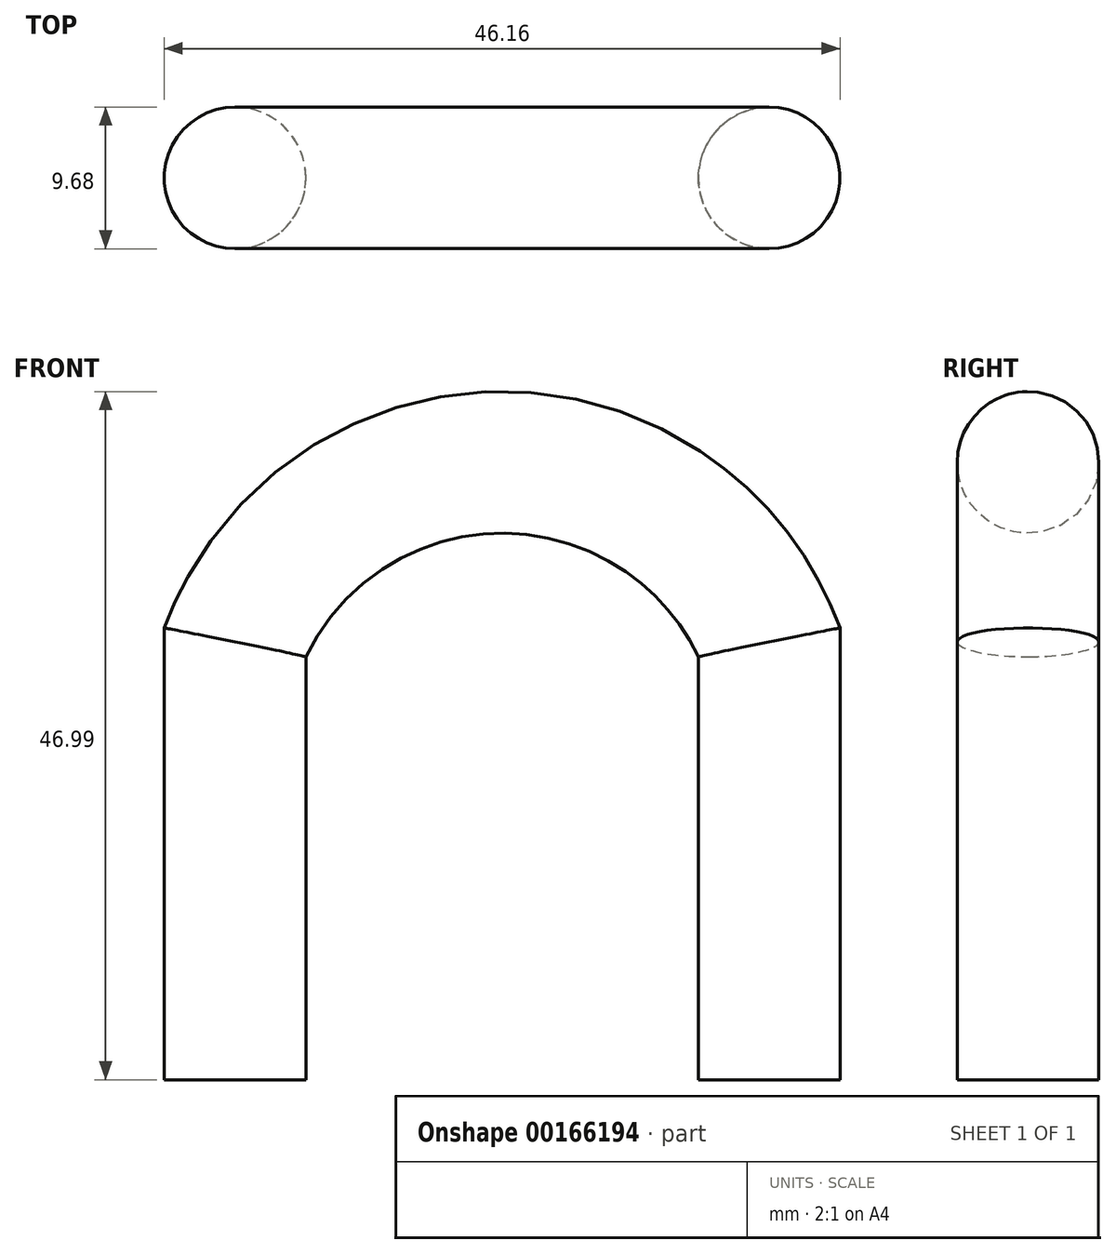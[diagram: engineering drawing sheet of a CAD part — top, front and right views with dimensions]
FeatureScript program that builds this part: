
annotation { "Feature Type Name" : "Feature", "Feature Type Description" : "" }
export const myFeature = defineFeature(function(context is Context, id is Id, definition is map)
    precondition{}
    {
        {
            var Q0;
            Q0=qCreatedBy(makeId("Front.planeOp"),FACE);
            var sketch = newSketch(context, id + "F0", { "sketchPlane" : qUnion([Q0])});
            skLineSegment(sketch, "E0", {"start": v(0, 0) * mm, "end": v(0, 29.9) * mm});
            skArc(sketch, "E1", {"start": v(36.48, 29.9) * mm, "mid": v(18.24, 42.15) * mm, "end": v(0, 29.9) * mm});
            skLineSegment(sketch, "E2", {"start": v(36.48, 29.9) * mm, "end": v(36.48, 0) * mm});
            skSolve(sketch);
        }
        {
            var Q0;
            Q0=qCreatedBy(makeId("Top.planeOp"),FACE);
            var sketch = newSketch(context, id + "F1", { "sketchPlane" : qUnion([Q0])});
            skCircle(sketch, "E3", {"center": v(0, 0) * mm, "radius": 4.84 * mm});
            skSolve(sketch);
        }
        {
            var Q0;
            Q0=makeQuery(id+"F1.imprint","IMPRINT",FACE,{"disambiguationData":[TD([[makeQuery(id+"F1.imprint","IMPRINT",EDGE,{"derivedFrom":sQuery(id+"F1.wireOp",EDGE,"E3")}),1.0]])]});
            var Q1;
            Q1=sQuery(id+"F0.wireOp",EDGE,"E0");
            var Q2;
            Q2=sQuery(id+"F0.wireOp",EDGE,"E1");
            var Q3;
            Q3=sQuery(id+"F0.wireOp",EDGE,"E2");
            sweep(context, id + "F2", {"profiles" : qUnion([Q0]), "path" : qUnion([Q1, Q2, Q3])});
        }
    });
